# Revit family: Faucet-Bath_Filler-KALLISTA-Script-P25088_1
name_source: partatom
category: Plumbing Fixtures
units: mm (PartAtom-declared; Revit-internal decimal feet)

## family parameters
Cut with Voids When Loaded = No
Host = Face
OmniClass Number = 23.31.11.00
OmniClass Title = Faucets
Part Type = Normal
Room Calculation Point = No
Round Connector Dimension = Use Diameter
Shared = No

## types (6) — shared parameters
ADA Compliant = No
Assembly Code = D2010
CW Connection = Yes
Cold Water Inlet = Cold Water Inlet
Date Modified = 10/30/2022
Default Elevation = 36"
Description = FREESTANDING BATH FAUCET, LESS HANDSHOWER
Drain Included = No
Faucet Hole Spacing = 0"
Flow Rate = 9 GPM
HW Connection = Yes
Handle Clearance = 3 1/4"
Height = 34 7/8"
Hot Water Inlet = Hot Water Inlet
Length = 9"
Manufacturer = Kallista Co.
Master Format 2014 = 22 41 39
Master Format 2014 Name = Residential Faucets, Supplies, and Trim
Material = Premium Metal Construction
Pressure = 0.00 psi
Product Documentation Link = https://resources.kohler.com
Product Name = Script
Spout Reach = 9"
URL = https://www.kallista.com
Vent Connection = No
Waste Connection = No
Waste Water Outlet = Waste Water Outlet
WaterSense Certified = No
Width = 4 5/16"

## per-type parameters (varying)
| type | Finish | Model | Product Page URL | Type |
| AD-Nickel Silver | Kallista-Metal-AD-Nickel_Silver | K-P25088-00-AD | https://www.kallista.com | 1 |
| BAF-Brushed French Gold | Kallista-Metal-BAF-Brushed_French_Gold | K-P25088-00-BAF | https://www.kallista.com | 2 |
| BN-Brushed Nickel | Kallista-Metal-BN-Brushed_Nickel | K-P25088-00-BN |  | 3 |
| BV-Brushed Bronze | Kallista-Metal-BV-Brushed_Bronze | K-P25088-00-BV | https://www.kallista.com | 4 |
| CP-Chrome | Kallista-Metal-CP-Chrome | K-P25088-00-CP | https://www.kallista.com | 5 |
| SN-Polished Nickel | Kallista-Metal-SN-Polished_Nickel | K-P25088-00-SN | https://www.kallista.com | 6 |

## geometry (parser evidence)
native form markers: Sweep x5
no freeform markers — native parametric forms only
